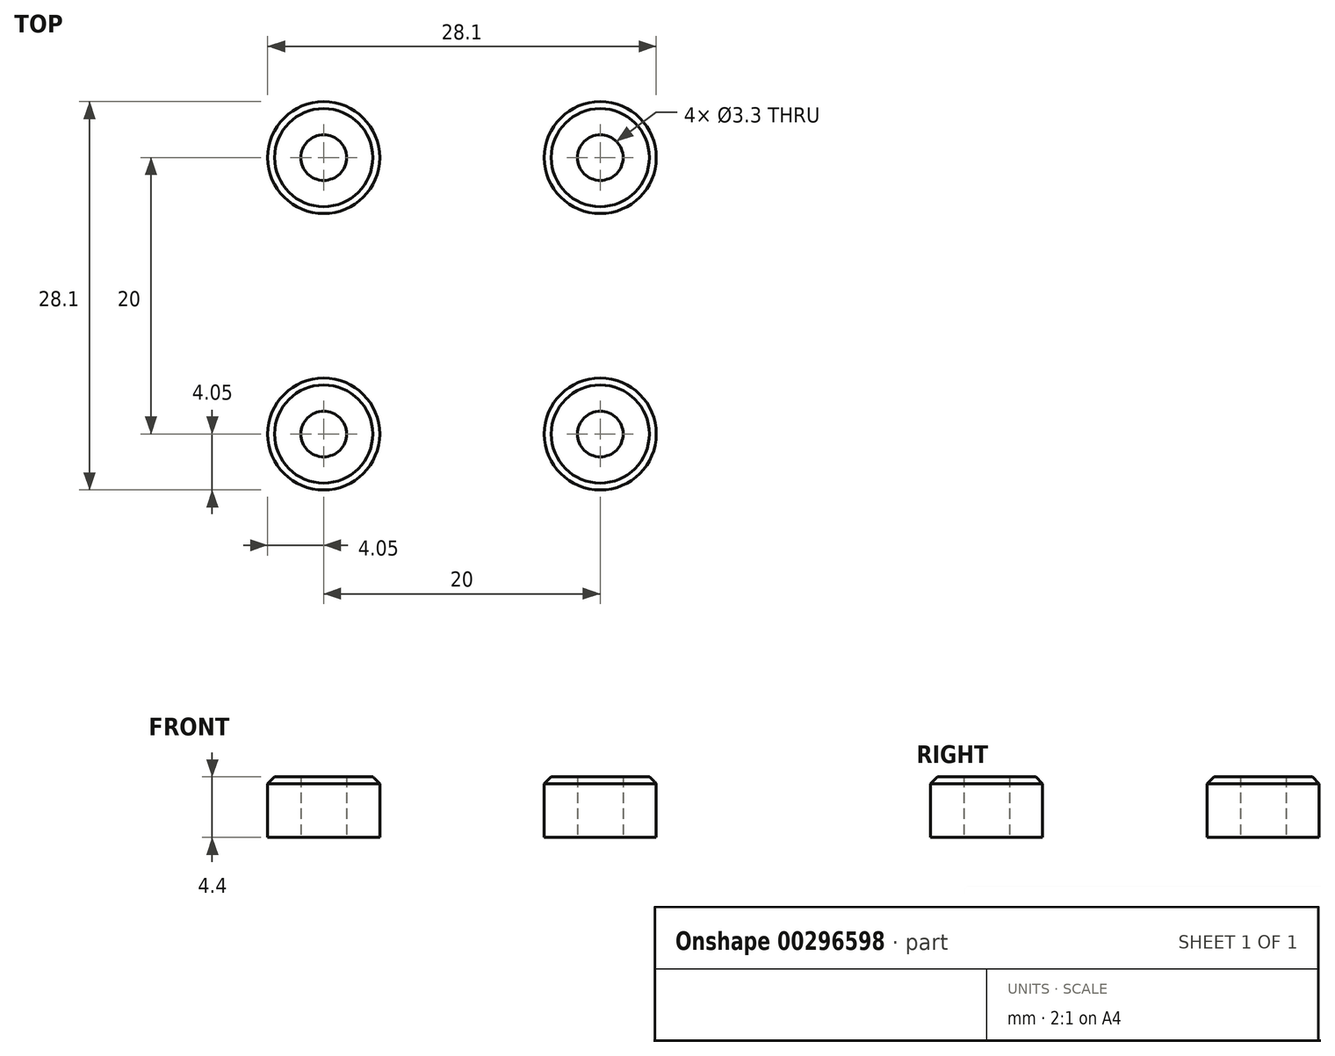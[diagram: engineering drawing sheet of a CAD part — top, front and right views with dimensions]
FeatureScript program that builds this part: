
annotation { "Feature Type Name" : "Feature", "Feature Type Description" : "" }
export const myFeature = defineFeature(function(context is Context, id is Id, definition is map)
    precondition{}
    {
        {
            var Q0;
            Q0=qCreatedBy(makeId("Top.planeOp"),FACE);
            var sketch = newSketch(context, id + "F0", { "sketchPlane" : qUnion([Q0])});
            skLineSegment(sketch, "E0.bottom", {"start": v(10, -10) * mm, "end": v(-10, -10) * mm, "construction": true});
            skLineSegment(sketch, "E0.top", {"start": v(10, 10) * mm, "end": v(-10, 10) * mm, "construction": true});
            skLineSegment(sketch, "E0.left", {"start": v(10, -10) * mm, "end": v(10, 10) * mm, "construction": true});
            skLineSegment(sketch, "E0.right", {"start": v(-10, -10) * mm, "end": v(-10, 10) * mm, "construction": true});
            skPoint(sketch, "E0.middle", {"position": v(0, 0) * mm});
            skCircle(sketch, "E1", {"center": v(-10, 10) * mm, "radius": 1.65 * mm});
            skCircle(sketch, "E2", {"center": v(-10, 10) * mm, "radius": 4.05 * mm});
            skCircle(sketch, "E3", {"center": v(10, 10) * mm, "radius": 1.65 * mm});
            skCircle(sketch, "E4", {"center": v(10, 10) * mm, "radius": 4.05 * mm});
            skCircle(sketch, "E5", {"center": v(10, -10) * mm, "radius": 1.65 * mm});
            skCircle(sketch, "E6", {"center": v(10, -10) * mm, "radius": 4.05 * mm});
            skCircle(sketch, "E7", {"center": v(-10, -10) * mm, "radius": 1.65 * mm});
            skCircle(sketch, "E8", {"center": v(-10, -10) * mm, "radius": 4.05 * mm});
            skSolve(sketch);
        }
        {
            var Q0;
            Q0 = qSketchRegion(id + "F0", true);
            extrude(context, id + "F1", {"entities" : qUnion([Q0]), "depth" : 4.4 * mm});
        }
        {
            var Q0;
            Q0=makeQuery(id+"F1.opExtrude","CAP_EDGE",EDGE,{"disambiguationData":[OSD([sQuery(id+"F0.wireOp",EDGE,"E2")])],"isStart":false});
            var Q1;
            Q1=makeQuery(id+"F1.opExtrude","CAP_EDGE",EDGE,{"disambiguationData":[OSD([sQuery(id+"F0.wireOp",EDGE,"E4")])],"isStart":false});
            var Q2;
            Q2=makeQuery(id+"F1.opExtrude","CAP_EDGE",EDGE,{"disambiguationData":[OSD([sQuery(id+"F0.wireOp",EDGE,"E6")])],"isStart":false});
            var Q3;
            Q3=makeQuery(id+"F1.opExtrude","CAP_EDGE",EDGE,{"disambiguationData":[OSD([sQuery(id+"F0.wireOp",EDGE,"E8")])],"isStart":false});
            chamfer(context, id + "F2", {"entities" : qUnion([Q0, Q1, Q2, Q3]), "width" : 0.5 * mm, "tangentPropagation" : true});
        }
    });
